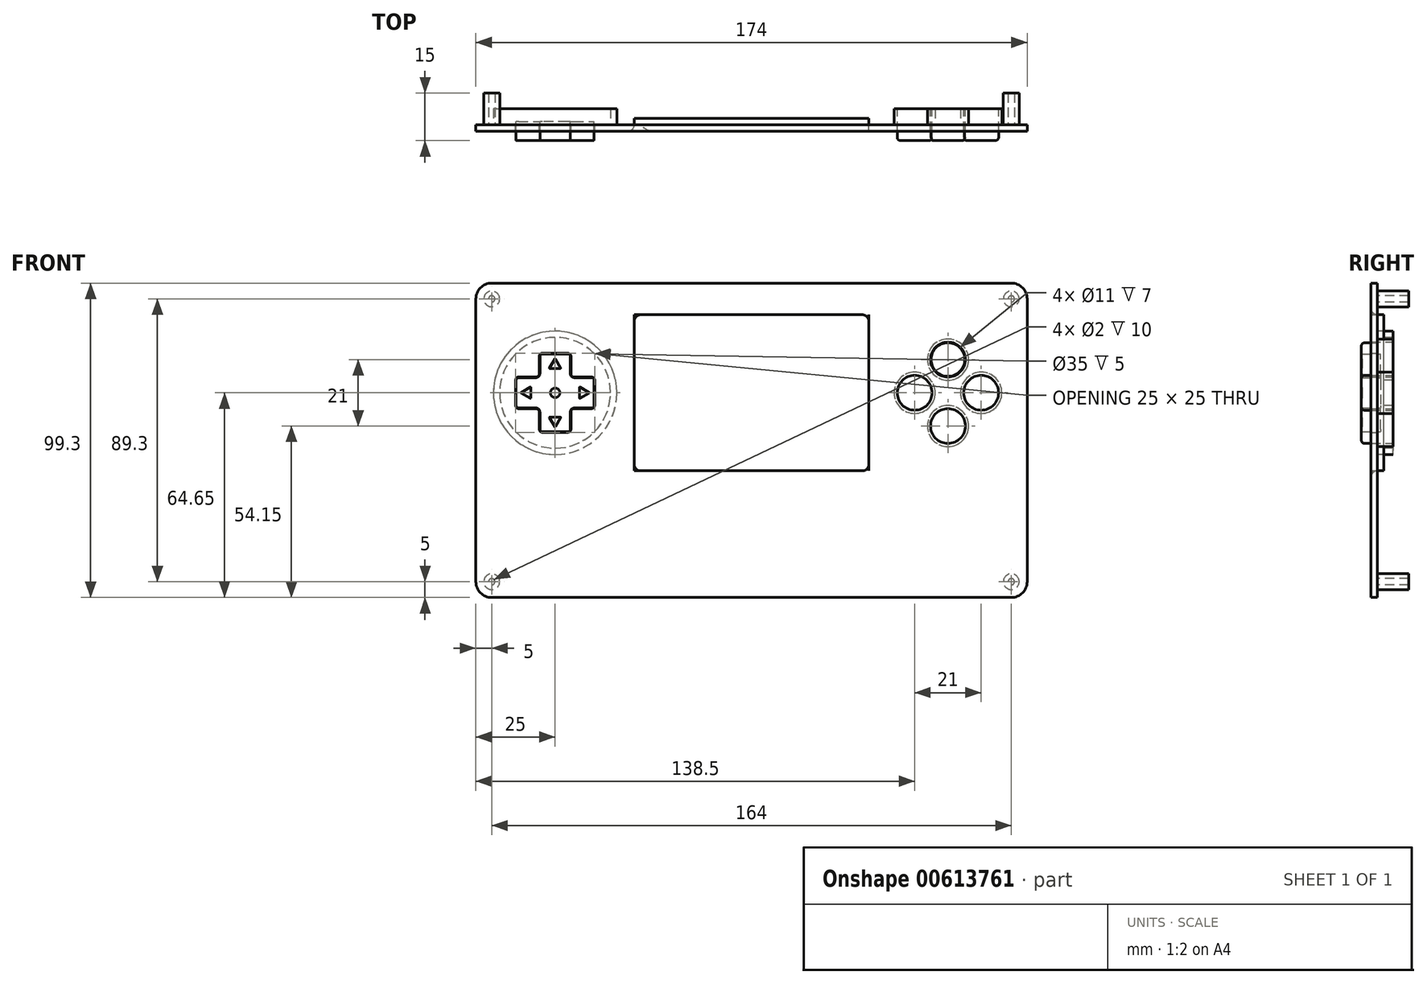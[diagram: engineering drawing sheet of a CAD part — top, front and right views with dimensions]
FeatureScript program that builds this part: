
annotation { "Feature Type Name" : "Feature", "Feature Type Description" : "" }
export const myFeature = defineFeature(function(context is Context, id is Id, definition is map)
    precondition{}
    {
        {
            var Q0;
            Q0=qCreatedBy(makeId("Front.planeOp"),FACE);
            var sketch = newSketch(context, id + "F0", { "sketchPlane" : qUnion([Q0])});
            skLineSegment(sketch, "E0.bottom", {"start": v(37, -24.65) * mm, "end": v(-37, -24.65) * mm});
            skLineSegment(sketch, "E0.top", {"start": v(37, 24.65) * mm, "end": v(-37, 24.65) * mm});
            skLineSegment(sketch, "E0.left", {"start": v(37, -24.65) * mm, "end": v(37, 24.65) * mm});
            skLineSegment(sketch, "E0.right", {"start": v(-37, -24.65) * mm, "end": v(-37, 24.65) * mm});
            skPoint(sketch, "E0.middle", {"position": v(0, 0) * mm});
            skLineSegment(sketch, "E1", {"start": v(-77.18, 0) * mm, "end": v(-77.18, 0) * mm});
            skPoint(sketch, "E1.startSnap0", {"position": v(-37, 0) * mm});
            skPoint(sketch, "E1.endSnap0", {"position": v(37, 0) * mm});
            skLineSegment(sketch, "E2.bottom", {"start": v(-57, -12.5) * mm, "end": v(-67, -12.5) * mm});
            skLineSegment(sketch, "E2.top", {"start": v(-57, 12.5) * mm, "end": v(-67, 12.5) * mm});
            skLineSegment(sketch, "E2.left", {"start": v(-57, -12.5) * mm, "end": v(-57, 12.5) * mm});
            skLineSegment(sketch, "E2.right", {"start": v(-67, -12.5) * mm, "end": v(-67, 12.5) * mm});
            skPoint(sketch, "E2.middle", {"position": v(-62, 0) * mm});
            skLineSegment(sketch, "E3.bottom", {"start": v(-74.5, 5) * mm, "end": v(-49.5, 5) * mm});
            skLineSegment(sketch, "E3.top", {"start": v(-74.5, -5) * mm, "end": v(-49.5, -5) * mm});
            skLineSegment(sketch, "E3.left", {"start": v(-74.5, 5) * mm, "end": v(-74.5, -5) * mm});
            skLineSegment(sketch, "E3.right", {"start": v(-49.5, 5) * mm, "end": v(-49.5, -5) * mm});
            skLineSegment(sketch, "E4", {"start": v(-67, 12.5) * mm, "end": v(80.57, 12.5) * mm, "construction": true});
            skLineSegment(sketch, "E5", {"start": v(37, 0) * mm, "end": v(62, 0) * mm, "construction": true});
            skLineSegment(sketch, "E6", {"start": v(62, 0) * mm, "end": v(62, 12.5) * mm, "construction": true});
            skCircle(sketch, "E7", {"center": v(-62, 0) * mm, "radius": 17.5 * mm});
            skLineSegment(sketch, "E8.bottom", {"start": v(-87, 34.65) * mm, "end": v(87, 34.65) * mm});
            skLineSegment(sketch, "E8.top", {"start": v(-87, -64.65) * mm, "end": v(87, -64.65) * mm});
            skLineSegment(sketch, "E8.left", {"start": v(-87, 34.65) * mm, "end": v(-87, -64.65) * mm});
            skLineSegment(sketch, "E8.right", {"start": v(87, 34.65) * mm, "end": v(87, -64.65) * mm});
            skPoint(sketch, "E9.center.orphan", {"position": v(62, 6.25) * mm});
            skCircle(sketch, "E10", {"center": v(62, 10.5) * mm, "radius": 5.5 * mm});
            skCircle(sketch, "E11.1.0", {"center": v(51.5, 0) * mm, "radius": 5.5 * mm});
            skCircle(sketch, "E11.2.0", {"center": v(62, -10.5) * mm, "radius": 5.5 * mm});
            skCircle(sketch, "E11.3.0", {"center": v(72.5, 0) * mm, "radius": 5.5 * mm});
            skPoint(sketch, "E11.center", {"position": v(62, 0) * mm});
            skSolve(sketch);
        }
        {
            var Q0;
            Q0=makeQuery(id+"F0.imprint","IMPRINT",FACE,{"disambiguationData":[TD([[makeQuery(id+"F0.imprint","IMPRINT",EDGE,{"derivedFrom":sQuery(id+"F0.wireOp",EDGE,"E0.bottom")}),1.0]])]});
            var Q1;
            {var subQ8=sQuery(id+"F0.wireOp",EDGE,"E2.bottom");Q1=makeQuery(id+"F0.imprint","IMPRINT",FACE,{"disambiguationData":[TD([[makeQuery(id+"F0.imprint","IMPRINT",EDGE,{"derivedFrom":subQ8}),1.0]])]});}
            extrude(context, id + "F1", {"entities" : qUnion([Q0, Q1]), "depth" : 2 * mm, "offsetDistance" : 25 * mm});
        }
        {
            var Q0;
            Q0=makeQuery(id+"F1.opExtrude","SWEPT_EDGE",EDGE,{"disambiguationData":[OSD([sQuery(id+"F0.wireOp",EDGE,"E2.top"),sQuery(id+"F0.wireOp",EDGE,"E2.right")])]});
            var Q1;
            Q1=makeQuery(id+"F1.opExtrude","SWEPT_EDGE",EDGE,{"disambiguationData":[OSD([sQuery(id+"F0.wireOp",EDGE,"E2.right"),sQuery(id+"F0.wireOp",EDGE,"E3.bottom")])]});
            var Q2;
            Q2=makeQuery(id+"F1.opExtrude","SWEPT_EDGE",EDGE,{"disambiguationData":[OSD([sQuery(id+"F0.wireOp",EDGE,"E3.bottom"),sQuery(id+"F0.wireOp",EDGE,"E3.left")])]});
            var Q3;
            Q3=makeQuery(id+"F1.opExtrude","SWEPT_EDGE",EDGE,{"disambiguationData":[OSD([sQuery(id+"F0.wireOp",EDGE,"E3.top"),sQuery(id+"F0.wireOp",EDGE,"E3.left")])]});
            var Q4;
            Q4=makeQuery(id+"F1.opExtrude","SWEPT_EDGE",EDGE,{"disambiguationData":[OSD([sQuery(id+"F0.wireOp",EDGE,"E2.right"),sQuery(id+"F0.wireOp",EDGE,"E3.top")])]});
            var Q5;
            Q5=makeQuery(id+"F1.opExtrude","SWEPT_EDGE",EDGE,{"disambiguationData":[OSD([sQuery(id+"F0.wireOp",EDGE,"E2.bottom"),sQuery(id+"F0.wireOp",EDGE,"E2.right")])]});
            var Q6;
            Q6=makeQuery(id+"F1.opExtrude","SWEPT_EDGE",EDGE,{"disambiguationData":[OSD([sQuery(id+"F0.wireOp",EDGE,"E2.bottom"),sQuery(id+"F0.wireOp",EDGE,"E2.left")])]});
            var Q7;
            Q7=makeQuery(id+"F1.opExtrude","SWEPT_EDGE",EDGE,{"disambiguationData":[OSD([sQuery(id+"F0.wireOp",EDGE,"E2.left"),sQuery(id+"F0.wireOp",EDGE,"E3.top")])]});
            var Q8;
            Q8=makeQuery(id+"F1.opExtrude","SWEPT_EDGE",EDGE,{"disambiguationData":[OSD([sQuery(id+"F0.wireOp",EDGE,"E3.top"),sQuery(id+"F0.wireOp",EDGE,"E3.right")])]});
            var Q9;
            Q9=makeQuery(id+"F1.opExtrude","SWEPT_EDGE",EDGE,{"disambiguationData":[OSD([sQuery(id+"F0.wireOp",EDGE,"E3.bottom"),sQuery(id+"F0.wireOp",EDGE,"E3.right")])]});
            var Q10;
            Q10=makeQuery(id+"F1.opExtrude","SWEPT_EDGE",EDGE,{"disambiguationData":[OSD([sQuery(id+"F0.wireOp",EDGE,"E2.left"),sQuery(id+"F0.wireOp",EDGE,"E3.bottom")])]});
            var Q11;
            Q11=makeQuery(id+"F1.opExtrude","SWEPT_EDGE",EDGE,{"disambiguationData":[OSD([sQuery(id+"F0.wireOp",EDGE,"E2.top"),sQuery(id+"F0.wireOp",EDGE,"E2.left")])]});
            fillet(context, id + "F2", {"entities" : qUnion([Q0, Q1, Q2, Q3, Q4, Q5, Q6, Q7, Q8, Q9, Q10, Q11]), "radius" : 1 * mm, "tangentPropagation" : true, "allowEdgeOverflow" : false});
        }
        {
            var Q0;
            Q0=makeQuery(id+"F1.opExtrude","SWEPT_EDGE",EDGE,{"disambiguationData":[OSD([sQuery(id+"F0.wireOp",EDGE,"E8.bottom"),sQuery(id+"F0.wireOp",EDGE,"E8.right")])]});
            var Q1;
            Q1=makeQuery(id+"F1.opExtrude","SWEPT_EDGE",EDGE,{"disambiguationData":[OSD([sQuery(id+"F0.wireOp",EDGE,"E8.top"),sQuery(id+"F0.wireOp",EDGE,"E8.right")])]});
            var Q2;
            Q2=makeQuery(id+"F1.opExtrude","SWEPT_EDGE",EDGE,{"disambiguationData":[OSD([sQuery(id+"F0.wireOp",EDGE,"E8.bottom"),sQuery(id+"F0.wireOp",EDGE,"E8.left")])]});
            var Q3;
            Q3=makeQuery(id+"F1.opExtrude","SWEPT_EDGE",EDGE,{"disambiguationData":[OSD([sQuery(id+"F0.wireOp",EDGE,"E8.top"),sQuery(id+"F0.wireOp",EDGE,"E8.left")])]});
            fillet(context, id + "F3", {"entities" : qUnion([Q0, Q1, Q2, Q3]), "radius" : 5 * mm, "tangentPropagation" : true, "allowEdgeOverflow" : false});
        }
        {
            var Q0;
            Q0=makeQuery(id+"F1.opExtrude","CAP_FACE",FACE,{"disambiguationData":[OSD([sQuery(id+"F0.wireOp",EDGE,"E0.bottom"),sQuery(id+"F0.wireOp",EDGE,"E0.top"),sQuery(id+"F0.wireOp",EDGE,"E0.left"),sQuery(id+"F0.wireOp",EDGE,"E0.right"),sQuery(id+"F0.wireOp",EDGE,"E2.bottom"),sQuery(id+"F0.wireOp",EDGE,"E2.top"),sQuery(id+"F0.wireOp",EDGE,"E2.left"),sQuery(id+"F0.wireOp",EDGE,"E2.right"),sQuery(id+"F0.wireOp",EDGE,"E3.bottom"),sQuery(id+"F0.wireOp",EDGE,"E3.top"),sQuery(id+"F0.wireOp",EDGE,"E3.left"),sQuery(id+"F0.wireOp",EDGE,"E3.right"),sQuery(id+"F0.wireOp",EDGE,"E8.bottom"),sQuery(id+"F0.wireOp",EDGE,"E8.top"),sQuery(id+"F0.wireOp",EDGE,"E8.left"),sQuery(id+"F0.wireOp",EDGE,"E8.right"),sQuery(id+"F0.wireOp",EDGE,"E10"),sQuery(id+"F0.wireOp",EDGE,"E11.1.0"),sQuery(id+"F0.wireOp",EDGE,"E11.2.0"),sQuery(id+"F0.wireOp",EDGE,"E11.3.0")])],"isStart":true});
            var sketch = newSketch(context, id + "F4", { "sketchPlane" : qUnion([Q0])});
            skCircle(sketch, "E12.0", {"center": v(-62, 10.5) * mm, "radius": 6.5 * mm});
            skCircle(sketch, "E13.0", {"center": v(-72.5, 0) * mm, "radius": 6.5 * mm});
            skCircle(sketch, "E14.0", {"center": v(-51.5, 0) * mm, "radius": 6.5 * mm});
            skCircle(sketch, "E15.0", {"center": v(-62, -10.5) * mm, "radius": 6.5 * mm});
            skSolve(sketch);
        }
        {
            var Q0;
            Q0=makeQuery(id+"F4.imprint","IMPRINT",FACE,{"disambiguationData":[TD([[makeQuery(id+"F4.imprint","IMPRINT",EDGE,{"derivedFrom":sQuery(id+"F4.wireOp",EDGE,"E12.0")}),1.0]])]});
            var Q1;
            Q1=makeQuery(id+"F4.imprint","IMPRINT",FACE,{"disambiguationData":[TD([[makeQuery(id+"F4.imprint","IMPRINT",EDGE,{"derivedFrom":sQuery(id+"F4.wireOp",EDGE,"E13.0")}),1.0]])]});
            var Q2;
            Q2=makeQuery(id+"F4.imprint","IMPRINT",FACE,{"disambiguationData":[TD([[makeQuery(id+"F4.imprint","IMPRINT",EDGE,{"derivedFrom":sQuery(id+"F4.wireOp",EDGE,"E14.0")}),1.0]])]});
            var Q3;
            Q3=makeQuery(id+"F4.imprint","IMPRINT",FACE,{"disambiguationData":[TD([[makeQuery(id+"F4.imprint","IMPRINT",EDGE,{"derivedFrom":sQuery(id+"F4.wireOp",EDGE,"E15.0")}),1.0]])]});
            extrude(context, id + "F5", {"entities" : qUnion([Q0, Q1, Q2, Q3]), "operationType" : NewBodyOperationType.ADD, "depth" : 5 * mm, "offsetDistance" : 25 * mm});
        }
        {
            var Q0;
            Q0=makeQuery(id+"F0.imprint","IMPRINT",FACE,{"disambiguationData":[TD([[makeQuery(id+"F0.imprint","IMPRINT",EDGE,{"derivedFrom":sQuery(id+"F0.wireOp",EDGE,"E0.bottom")}),1.0]])]});
            var sketch = newSketch(context, id + "F6", { "sketchPlane" : qUnion([Q0])});
            skCircle(sketch, "E16.0", {"center": v(-62, 0) * mm, "radius": 19.5 * mm});
            skCircle(sketch, "E17.0", {"center": v(-62, 0) * mm, "radius": 17.5 * mm});
            skSolve(sketch);
        }
        {
            var Q0;
            Q0 = qSketchRegion(id + "F6", true);
            var Q1;
            Q1=makeQuery(id+"F5.opExtrude","CAP_FACE",FACE,{"disambiguationData":[OSD([sQuery(id+"F0.wireOp",EDGE,"E11.1.0"),sQuery(id+"F4.wireOp",EDGE,"E14.0")])],"isStart":false});
            extrude(context, id + "F7", {"entities" : qUnion([Q0]), "operationType" : NewBodyOperationType.ADD, "endBound" : BoundingType.UP_TO_SURFACE, "oppositeDirection" : true, "depth" : 25 * mm, "endBoundEntityFace" : qUnion([Q1]), "offsetDistance" : 25 * mm});
        }
        {
            var Q0;
            Q0=makeQuery(id+"F1.opExtrude","SWEPT_EDGE",EDGE,{"disambiguationData":[OSD([sQuery(id+"F0.wireOp",EDGE,"E0.top"),sQuery(id+"F0.wireOp",EDGE,"E0.right")])]});
            var Q1;
            Q1=makeQuery(id+"F1.opExtrude","SWEPT_EDGE",EDGE,{"disambiguationData":[OSD([sQuery(id+"F0.wireOp",EDGE,"E0.top"),sQuery(id+"F0.wireOp",EDGE,"E0.left")])]});
            var Q2;
            Q2=makeQuery(id+"F1.opExtrude","SWEPT_EDGE",EDGE,{"disambiguationData":[OSD([sQuery(id+"F0.wireOp",EDGE,"E0.bottom"),sQuery(id+"F0.wireOp",EDGE,"E0.left")])]});
            var Q3;
            Q3=makeQuery(id+"F1.opExtrude","SWEPT_EDGE",EDGE,{"disambiguationData":[OSD([sQuery(id+"F0.wireOp",EDGE,"E0.bottom"),sQuery(id+"F0.wireOp",EDGE,"E0.right")])]});
            var Q4;
            Q4=makeQuery(id+"F1.opExtrude","CAP_EDGE",EDGE,{"disambiguationData":[OSD([sQuery(id+"F0.wireOp",EDGE,"E0.right")])],"isStart":false});
            fillet(context, id + "F8", {"entities" : qUnion([Q0, Q1, Q2, Q3, Q4]), "radius" : 2 * mm, "tangentPropagation" : true, "allowEdgeOverflow" : false});
        }
        {
            var Q0;
            Q0=makeQuery(id+"F0.imprint","IMPRINT",FACE,{"disambiguationData":[TD([[makeQuery(id+"F0.imprint","IMPRINT",EDGE,{"derivedFrom":sQuery(id+"F0.wireOp",EDGE,"E0.bottom")}),1.0]])]});
            var sketch = newSketch(context, id + "F9", { "sketchPlane" : qUnion([Q0])});
            skLineSegment(sketch, "E18.0", {"start": v(-82, 29.65) * mm, "end": v(-82, -59.65) * mm, "construction": true});
            skLineSegment(sketch, "E18.1", {"start": v(82, 29.65) * mm, "end": v(-82, 29.65) * mm, "construction": true});
            skLineSegment(sketch, "E18.2", {"start": v(82, -59.65) * mm, "end": v(82, 29.65) * mm, "construction": true});
            skLineSegment(sketch, "E18.3", {"start": v(-82, -59.65) * mm, "end": v(82, -59.65) * mm, "construction": true});
            skCircle(sketch, "E19", {"center": v(82, 29.65) * mm, "radius": 1 * mm});
            skCircle(sketch, "E20", {"center": v(-82, 29.65) * mm, "radius": 1 * mm});
            skCircle(sketch, "E21", {"center": v(-82, -59.65) * mm, "radius": 1 * mm});
            skCircle(sketch, "E22", {"center": v(82, -59.65) * mm, "radius": 1 * mm});
            skCircle(sketch, "E23", {"center": v(82, -59.65) * mm, "radius": 2.5 * mm});
            skCircle(sketch, "E24", {"center": v(82, 29.65) * mm, "radius": 2.5 * mm});
            skCircle(sketch, "E25", {"center": v(-82, 29.65) * mm, "radius": 2.5 * mm});
            skCircle(sketch, "E26", {"center": v(-82, -59.65) * mm, "radius": 2.5 * mm});
            skSolve(sketch);
        }
        {
            var Q0;
            Q0=makeQuery(id+"F9.imprint","IMPRINT",FACE,{"disambiguationData":[TD([[makeQuery(id+"F9.imprint","IMPRINT",EDGE,{"derivedFrom":sQuery(id+"F9.wireOp",EDGE,"E19")}),-1.0]])]});
            var Q1;
            Q1=makeQuery(id+"F9.imprint","IMPRINT",FACE,{"disambiguationData":[TD([[makeQuery(id+"F9.imprint","IMPRINT",EDGE,{"derivedFrom":sQuery(id+"F9.wireOp",EDGE,"E20")}),-1.0]])]});
            var Q2;
            Q2=makeQuery(id+"F9.imprint","IMPRINT",FACE,{"disambiguationData":[TD([[makeQuery(id+"F9.imprint","IMPRINT",EDGE,{"derivedFrom":sQuery(id+"F9.wireOp",EDGE,"E21")}),-1.0]])]});
            var Q3;
            Q3=makeQuery(id+"F9.imprint","IMPRINT",FACE,{"disambiguationData":[TD([[makeQuery(id+"F9.imprint","IMPRINT",EDGE,{"derivedFrom":sQuery(id+"F9.wireOp",EDGE,"E22")}),-1.0]])]});
            extrude(context, id + "F10", {"entities" : qUnion([Q0, Q1, Q2, Q3]), "operationType" : NewBodyOperationType.ADD, "oppositeDirection" : true, "depth" : 10 * mm, "offsetDistance" : 25 * mm});
        }
        {
            var Q0;
            Q0=makeQuery(id+"F0.imprint","IMPRINT",FACE,{"disambiguationData":[TD([[makeQuery(id+"F0.imprint","IMPRINT",EDGE,{"derivedFrom":sQuery(id+"F0.wireOp",EDGE,"E0.bottom")}),-1.0]])]});
            extrude(context, id + "F11", {"entities" : qUnion([Q0]), "oppositeDirection" : true, "depth" : 2 * mm, "offsetDistance" : 25 * mm});
        }
        {
            var Q0;
            Q0=makeQuery(id+"F1.opExtrude","CAP_FACE",FACE,{"disambiguationData":[OSD([sQuery(id+"F0.wireOp",EDGE,"E0.bottom"),sQuery(id+"F0.wireOp",EDGE,"E0.top"),sQuery(id+"F0.wireOp",EDGE,"E0.left"),sQuery(id+"F0.wireOp",EDGE,"E0.right"),sQuery(id+"F0.wireOp",EDGE,"E2.bottom"),sQuery(id+"F0.wireOp",EDGE,"E2.top"),sQuery(id+"F0.wireOp",EDGE,"E2.left"),sQuery(id+"F0.wireOp",EDGE,"E2.right"),sQuery(id+"F0.wireOp",EDGE,"E3.bottom"),sQuery(id+"F0.wireOp",EDGE,"E3.top"),sQuery(id+"F0.wireOp",EDGE,"E3.left"),sQuery(id+"F0.wireOp",EDGE,"E3.right"),sQuery(id+"F0.wireOp",EDGE,"E8.bottom"),sQuery(id+"F0.wireOp",EDGE,"E8.top"),sQuery(id+"F0.wireOp",EDGE,"E8.left"),sQuery(id+"F0.wireOp",EDGE,"E8.right"),sQuery(id+"F0.wireOp",EDGE,"E10"),sQuery(id+"F0.wireOp",EDGE,"E11.1.0"),sQuery(id+"F0.wireOp",EDGE,"E11.2.0"),sQuery(id+"F0.wireOp",EDGE,"E11.3.0")])],"isStart":false});
            var sketch = newSketch(context, id + "F12", { "sketchPlane" : qUnion([Q0])});
            skArc(sketch, "E27.0", {"start": v(-68, 4.8) * mm, "mid": v(-67.15, 5.15) * mm, "end": v(-66.8, 6) * mm});
            skLineSegment(sketch, "E27.1", {"start": v(-56, -4.8) * mm, "end": v(-50.5, -4.8) * mm});
            skArc(sketch, "E27.2", {"start": v(-49.7, -4) * mm, "mid": v(-49.93, -4.57) * mm, "end": v(-50.5, -4.8) * mm});
            skLineSegment(sketch, "E27.3", {"start": v(-49.7, 4) * mm, "end": v(-49.7, -4) * mm});
            skArc(sketch, "E27.4", {"start": v(-50.5, 4.8) * mm, "mid": v(-49.93, 4.57) * mm, "end": v(-49.7, 4) * mm});
            skLineSegment(sketch, "E27.5", {"start": v(-56, 4.8) * mm, "end": v(-50.5, 4.8) * mm});
            skArc(sketch, "E27.6", {"start": v(-57.2, 6) * mm, "mid": v(-56.85, 5.15) * mm, "end": v(-56, 4.8) * mm});
            skArc(sketch, "E27.7", {"start": v(-66.8, 11.5) * mm, "mid": v(-66.57, 12.07) * mm, "end": v(-66, 12.3) * mm});
            skLineSegment(sketch, "E27.8", {"start": v(-58, 12.3) * mm, "end": v(-66, 12.3) * mm});
            skArc(sketch, "E27.9", {"start": v(-58, 12.3) * mm, "mid": v(-57.43, 12.07) * mm, "end": v(-57.2, 11.5) * mm});
            skLineSegment(sketch, "E27.10", {"start": v(-57.2, 6) * mm, "end": v(-57.2, 11.5) * mm});
            skArc(sketch, "E27.11", {"start": v(-56, -4.8) * mm, "mid": v(-56.85, -5.15) * mm, "end": v(-57.2, -6) * mm});
            skLineSegment(sketch, "E27.12", {"start": v(-66.8, 6) * mm, "end": v(-66.8, 11.5) * mm});
            skLineSegment(sketch, "E27.13", {"start": v(-57.2, -11.5) * mm, "end": v(-57.2, -6) * mm});
            skArc(sketch, "E27.14", {"start": v(-57.2, -11.5) * mm, "mid": v(-57.43, -12.07) * mm, "end": v(-58, -12.3) * mm});
            skLineSegment(sketch, "E27.15", {"start": v(-58, -12.3) * mm, "end": v(-66, -12.3) * mm});
            skArc(sketch, "E27.16", {"start": v(-66, -12.3) * mm, "mid": v(-66.57, -12.07) * mm, "end": v(-66.8, -11.5) * mm});
            skLineSegment(sketch, "E27.17", {"start": v(-66.8, -11.5) * mm, "end": v(-66.8, -6) * mm});
            skArc(sketch, "E27.18", {"start": v(-66.8, -6) * mm, "mid": v(-67.15, -5.15) * mm, "end": v(-68, -4.8) * mm});
            skLineSegment(sketch, "E27.19", {"start": v(-73.5, -4.8) * mm, "end": v(-68, -4.8) * mm});
            skArc(sketch, "E27.20", {"start": v(-73.5, -4.8) * mm, "mid": v(-74.07, -4.57) * mm, "end": v(-74.3, -4) * mm});
            skLineSegment(sketch, "E27.21", {"start": v(-74.3, 4) * mm, "end": v(-74.3, -4) * mm});
            skArc(sketch, "E27.22", {"start": v(-74.3, 4) * mm, "mid": v(-74.07, 4.57) * mm, "end": v(-73.5, 4.8) * mm});
            skLineSegment(sketch, "E27.23", {"start": v(-73.5, 4.8) * mm, "end": v(-68, 4.8) * mm});
            skSolve(sketch);
        }
        {
            var Q0;
            Q0=makeQuery(id+"F12.imprint","IMPRINT",FACE,{"disambiguationData":[TD([[makeQuery(id+"F12.imprint","IMPRINT",EDGE,{"derivedFrom":sQuery(id+"F12.wireOp",EDGE,"E27.0")}),-1.0]])]});
            extrude(context, id + "F13", {"entities" : qUnion([Q0]), "depth" : 3 * mm, "offsetDistance" : 25 * mm, "hasSecondDirection" : true, "secondDirectionOppositeDirection" : true, "secondDirectionDepth" : 3 * mm});
        }
        {
            var Q0;
            Q0=makeQuery(id+"F1.opExtrude","CAP_FACE",FACE,{"disambiguationData":[OSD([sQuery(id+"F0.wireOp",EDGE,"E0.bottom"),sQuery(id+"F0.wireOp",EDGE,"E0.top"),sQuery(id+"F0.wireOp",EDGE,"E0.left"),sQuery(id+"F0.wireOp",EDGE,"E0.right"),sQuery(id+"F0.wireOp",EDGE,"E2.bottom"),sQuery(id+"F0.wireOp",EDGE,"E2.top"),sQuery(id+"F0.wireOp",EDGE,"E2.left"),sQuery(id+"F0.wireOp",EDGE,"E2.right"),sQuery(id+"F0.wireOp",EDGE,"E3.bottom"),sQuery(id+"F0.wireOp",EDGE,"E3.top"),sQuery(id+"F0.wireOp",EDGE,"E3.left"),sQuery(id+"F0.wireOp",EDGE,"E3.right"),sQuery(id+"F0.wireOp",EDGE,"E8.bottom"),sQuery(id+"F0.wireOp",EDGE,"E8.top"),sQuery(id+"F0.wireOp",EDGE,"E8.left"),sQuery(id+"F0.wireOp",EDGE,"E8.right"),sQuery(id+"F0.wireOp",EDGE,"E10"),sQuery(id+"F0.wireOp",EDGE,"E11.1.0"),sQuery(id+"F0.wireOp",EDGE,"E11.2.0"),sQuery(id+"F0.wireOp",EDGE,"E11.3.0")])],"isStart":false});
            var sketch = newSketch(context, id + "F14", { "sketchPlane" : qUnion([Q0])});
            skCircle(sketch, "E28.0", {"center": v(62, 10.5) * mm, "radius": 5.3 * mm});
            skCircle(sketch, "E29.0", {"center": v(51.5, 0) * mm, "radius": 5.7 * mm});
            skCircle(sketch, "E30.0", {"center": v(72.5, 0) * mm, "radius": 5.7 * mm});
            skCircle(sketch, "E31.0", {"center": v(62, -10.5) * mm, "radius": 5.7 * mm});
            skSolve(sketch);
        }
        {
            var Q0;
            Q0=makeQuery(id+"F14.imprint","IMPRINT",FACE,{"disambiguationData":[TD([[makeQuery(id+"F14.imprint","IMPRINT",EDGE,{"derivedFrom":sQuery(id+"F14.wireOp",EDGE,"E28.0")}),1.0]])]});
            var Q1;
            Q1=makeQuery(id+"F14.imprint","IMPRINT",FACE,{"disambiguationData":[TD([[makeQuery(id+"F14.imprint","IMPRINT",EDGE,{"derivedFrom":makeQuery(id+"F1.opExtrude","CAP_EDGE",EDGE,{"disambiguationData":[OSD([sQuery(id+"F0.wireOp",EDGE,"E11.1.0")])],"isStart":false})}),1.0]])]});
            var Q2;
            Q2=makeQuery(id+"F14.imprint","IMPRINT",FACE,{"disambiguationData":[TD([[makeQuery(id+"F14.imprint","IMPRINT",EDGE,{"derivedFrom":makeQuery(id+"F1.opExtrude","CAP_EDGE",EDGE,{"disambiguationData":[OSD([sQuery(id+"F0.wireOp",EDGE,"E11.3.0")])],"isStart":false})}),1.0]])]});
            var Q3;
            Q3=makeQuery(id+"F14.imprint","IMPRINT",FACE,{"disambiguationData":[TD([[makeQuery(id+"F14.imprint","IMPRINT",EDGE,{"derivedFrom":makeQuery(id+"F1.opExtrude","CAP_EDGE",EDGE,{"disambiguationData":[OSD([sQuery(id+"F0.wireOp",EDGE,"E11.2.0")])],"isStart":false})}),1.0]])]});
            extrude(context, id + "F15", {"entities" : qUnion([Q0, Q1, Q2, Q3]), "depth" : 3 * mm, "offsetDistance" : 25 * mm, "hasSecondDirection" : true, "secondDirectionOppositeDirection" : true, "secondDirectionDepth" : 2 * mm});
        }
        {
            var Q0;
            Q0=makeQuery(id+"F15.opExtrude","CAP_EDGE",EDGE,{"disambiguationData":[OSD([sQuery(id+"F14.wireOp",EDGE,"E28.0")])],"isStart":false});
            var Q1;
            Q1=makeQuery(id+"F15.opExtrude","CAP_EDGE",EDGE,{"disambiguationData":[OSD([sQuery(id+"F0.wireOp",EDGE,"E11.1.0")])],"isStart":false});
            var Q2;
            Q2=makeQuery(id+"F15.opExtrude","CAP_EDGE",EDGE,{"disambiguationData":[OSD([sQuery(id+"F0.wireOp",EDGE,"E11.3.0")])],"isStart":false});
            var Q3;
            Q3=makeQuery(id+"F15.opExtrude","CAP_FACE",FACE,{"disambiguationData":[OSD([sQuery(id+"F0.wireOp",EDGE,"E11.2.0")])],"isStart":false});
            fillet(context, id + "F16", {"entities" : qUnion([Q0, Q1, Q2, Q3]), "radius" : 1 * mm, "tangentPropagation" : true, "allowEdgeOverflow" : false});
        }
        {
            var Q0;
            Q0=makeQuery(id+"F13.opExtrude","CAP_FACE",FACE,{"disambiguationData":[OSD([sQuery(id+"F12.wireOp",EDGE,"E27.0"),sQuery(id+"F12.wireOp",EDGE,"E27.1"),sQuery(id+"F12.wireOp",EDGE,"E27.2"),sQuery(id+"F12.wireOp",EDGE,"E27.3"),sQuery(id+"F12.wireOp",EDGE,"E27.4"),sQuery(id+"F12.wireOp",EDGE,"E27.5"),sQuery(id+"F12.wireOp",EDGE,"E27.6"),sQuery(id+"F12.wireOp",EDGE,"E27.7"),sQuery(id+"F12.wireOp",EDGE,"E27.8"),sQuery(id+"F12.wireOp",EDGE,"E27.9"),sQuery(id+"F12.wireOp",EDGE,"E27.10"),sQuery(id+"F12.wireOp",EDGE,"E27.11"),sQuery(id+"F12.wireOp",EDGE,"E27.12"),sQuery(id+"F12.wireOp",EDGE,"E27.13"),sQuery(id+"F12.wireOp",EDGE,"E27.14"),sQuery(id+"F12.wireOp",EDGE,"E27.15"),sQuery(id+"F12.wireOp",EDGE,"E27.16"),sQuery(id+"F12.wireOp",EDGE,"E27.17"),sQuery(id+"F12.wireOp",EDGE,"E27.18"),sQuery(id+"F12.wireOp",EDGE,"E27.19"),sQuery(id+"F12.wireOp",EDGE,"E27.20"),sQuery(id+"F12.wireOp",EDGE,"E27.21"),sQuery(id+"F12.wireOp",EDGE,"E27.22"),sQuery(id+"F12.wireOp",EDGE,"E27.23")])],"isStart":false});
            var sketch = newSketch(context, id + "F17", { "sketchPlane" : qUnion([Q0])});
            skLineSegment(sketch, "E32", {"start": v(-74.3, 0) * mm, "end": v(-49.7, 0) * mm, "construction": true});
            skLineSegment(sketch, "E33", {"start": v(-62, 12.3) * mm, "end": v(-62, -12.3) * mm, "construction": true});
            skLineSegment(sketch, "E34.cCircle", {"start": v(-62, 6.6) * mm, "end": v(-62, 6.6) * mm});
            skPoint(sketch, "E34.cCircle.centerSnap0", {"position": v(-57.2, 8.75) * mm});
            skLineSegment(sketch, "E34.1", {"start": v(-62, 6.6) * mm, "end": v(-62, 6.6) * mm});
            skPoint(sketch, "E34.0.midPoint", {"position": v(-60.14, 9.82) * mm});
            skCircle(sketch, "E35.cCircle", {"center": v(-53.25, 0) * mm, "radius": 1.07 * mm, "construction": true});
            skPoint(sketch, "E35.cCircle.centerSnap0", {"position": v(-53.25, -4.8) * mm});
            skLineSegment(sketch, "E35.0", {"start": v(-54.32, -1.86) * mm, "end": v(-54.32, 1.86) * mm});
            skLineSegment(sketch, "E35.1", {"start": v(-54.32, 1.86) * mm, "end": v(-51.1, 0) * mm});
            skLineSegment(sketch, "E35.2", {"start": v(-51.1, 0) * mm, "end": v(-54.32, -1.86) * mm});
            skPoint(sketch, "E35.0.midPoint", {"position": v(-54.32, 0) * mm});
            skPoint(sketch, "E36.orphan", {"position": v(-65.72, 6.6) * mm});
            skPoint(sketch, "E37.orphan", {"position": v(-58.28, 6.6) * mm});
            skPoint(sketch, "E34.2.end.orphan", {"position": v(-62, 13.04) * mm});
            skLineSegment(sketch, "E38.1.0", {"start": v(-63.86, 7.68) * mm, "end": v(-62, 10.9) * mm});
            skLineSegment(sketch, "E38.1.1", {"start": v(-60.14, 7.68) * mm, "end": v(-63.86, 7.68) * mm});
            skLineSegment(sketch, "E38.1.2", {"start": v(-62, 10.9) * mm, "end": v(-60.14, 7.68) * mm});
            skLineSegment(sketch, "E38.2.0", {"start": v(-69.68, -1.86) * mm, "end": v(-72.9, 0) * mm});
            skLineSegment(sketch, "E38.2.1", {"start": v(-69.68, 1.86) * mm, "end": v(-69.68, -1.86) * mm});
            skLineSegment(sketch, "E38.2.2", {"start": v(-72.9, 0) * mm, "end": v(-69.68, 1.86) * mm});
            skLineSegment(sketch, "E38.3.0", {"start": v(-60.14, -7.68) * mm, "end": v(-62, -10.9) * mm});
            skLineSegment(sketch, "E38.3.1", {"start": v(-63.86, -7.68) * mm, "end": v(-60.14, -7.68) * mm});
            skLineSegment(sketch, "E38.3.2", {"start": v(-62, -10.9) * mm, "end": v(-63.86, -7.68) * mm});
            skPoint(sketch, "E38.center", {"position": v(-62, 0) * mm});
            skCircle(sketch, "E39", {"center": v(-62, 0) * mm, "radius": 1.5 * mm});
            skSolve(sketch);
        }
        {
            var Q0;
            Q0=makeQuery(id+"F17.imprint","IMPRINT",FACE,{"disambiguationData":[TD([[makeQuery(id+"F17.imprint","IMPRINT",EDGE,{"derivedFrom":sQuery(id+"F17.wireOp",EDGE,"E38.1.0")}),-1.0]])]});
            var Q1;
            Q1=makeQuery(id+"F17.imprint","IMPRINT",FACE,{"disambiguationData":[TD([[makeQuery(id+"F17.imprint","IMPRINT",EDGE,{"derivedFrom":sQuery(id+"F17.wireOp",EDGE,"E35.0")}),-1.0]])]});
            var Q2;
            Q2=makeQuery(id+"F17.imprint","IMPRINT",FACE,{"disambiguationData":[TD([[makeQuery(id+"F17.imprint","IMPRINT",EDGE,{"derivedFrom":sQuery(id+"F17.wireOp",EDGE,"E38.3.0")}),-1.0]])]});
            var Q3;
            Q3=makeQuery(id+"F17.imprint","IMPRINT",FACE,{"disambiguationData":[TD([[makeQuery(id+"F17.imprint","IMPRINT",EDGE,{"derivedFrom":sQuery(id+"F17.wireOp",EDGE,"E38.2.0")}),-1.0]])]});
            var Q4;
            Q4=makeQuery(id+"F17.imprint","IMPRINT",FACE,{"disambiguationData":[TD([[makeQuery(id+"F17.imprint","IMPRINT",EDGE,{"derivedFrom":sQuery(id+"F17.wireOp",EDGE,"E39")}),1.0]])]});
            extrude(context, id + "F18", {"entities" : qUnion([Q0, Q1, Q2, Q3, Q4]), "operationType" : NewBodyOperationType.REMOVE, "oppositeDirection" : true, "depth" : .2 * mm, "offsetDistance" : 25 * mm});
        }
        {
            var Q0;
            Q0=makeQuery(id+"F18.boolean.opBoolean","COPY",EDGE,{"derivedFrom":makeQuery(id+"F18.opExtrude","CAP_EDGE",EDGE,{"disambiguationData":[OSD([sQuery(id+"F17.wireOp",EDGE,"E39")])],"isStart":false})});
            var Q1;
            Q1=makeQuery(id+"F13.opExtrude","CAP_FACE",FACE,{"disambiguationData":[OSD([sQuery(id+"F12.wireOp",EDGE,"E27.0"),sQuery(id+"F12.wireOp",EDGE,"E27.1"),sQuery(id+"F12.wireOp",EDGE,"E27.2"),sQuery(id+"F12.wireOp",EDGE,"E27.3"),sQuery(id+"F12.wireOp",EDGE,"E27.4"),sQuery(id+"F12.wireOp",EDGE,"E27.5"),sQuery(id+"F12.wireOp",EDGE,"E27.6"),sQuery(id+"F12.wireOp",EDGE,"E27.7"),sQuery(id+"F12.wireOp",EDGE,"E27.8"),sQuery(id+"F12.wireOp",EDGE,"E27.9"),sQuery(id+"F12.wireOp",EDGE,"E27.10"),sQuery(id+"F12.wireOp",EDGE,"E27.11"),sQuery(id+"F12.wireOp",EDGE,"E27.12"),sQuery(id+"F12.wireOp",EDGE,"E27.13"),sQuery(id+"F12.wireOp",EDGE,"E27.14"),sQuery(id+"F12.wireOp",EDGE,"E27.15"),sQuery(id+"F12.wireOp",EDGE,"E27.16"),sQuery(id+"F12.wireOp",EDGE,"E27.17"),sQuery(id+"F12.wireOp",EDGE,"E27.18"),sQuery(id+"F12.wireOp",EDGE,"E27.19"),sQuery(id+"F12.wireOp",EDGE,"E27.20"),sQuery(id+"F12.wireOp",EDGE,"E27.21"),sQuery(id+"F12.wireOp",EDGE,"E27.22"),sQuery(id+"F12.wireOp",EDGE,"E27.23")])],"isStart":false});
            var Q2;
            Q2=makeQuery(id+"F18.boolean.opBoolean","COPY",EDGE,{"derivedFrom":makeQuery(id+"F18.opExtrude","CAP_EDGE",EDGE,{"disambiguationData":[OSD([sQuery(id+"F17.wireOp",EDGE,"E38.1.1")])],"isStart":true})});
            var Q3;
            Q3=makeQuery(id+"F18.boolean.opBoolean","COPY",EDGE,{"derivedFrom":makeQuery(id+"F18.opExtrude","CAP_EDGE",EDGE,{"disambiguationData":[OSD([sQuery(id+"F17.wireOp",EDGE,"E38.1.0")])],"isStart":true})});
            var Q4;
            Q4=makeQuery(id+"F18.boolean.opBoolean","COPY",EDGE,{"derivedFrom":makeQuery(id+"F18.opExtrude","CAP_EDGE",EDGE,{"disambiguationData":[OSD([sQuery(id+"F17.wireOp",EDGE,"E38.1.2")])],"isStart":true})});
            var Q5;
            Q5=makeQuery(id+"F18.boolean.opBoolean","COPY",EDGE,{"derivedFrom":makeQuery(id+"F18.opExtrude","SWEPT_EDGE",EDGE,{"disambiguationData":[OSD([sQuery(id+"F17.wireOp",EDGE,"E38.1.0"),sQuery(id+"F17.wireOp",EDGE,"E38.1.1")])]})});
            var Q6;
            Q6=makeQuery(id+"F18.boolean.opBoolean","COPY",EDGE,{"derivedFrom":makeQuery(id+"F18.opExtrude","SWEPT_EDGE",EDGE,{"disambiguationData":[OSD([sQuery(id+"F17.wireOp",EDGE,"E38.1.0"),sQuery(id+"F17.wireOp",EDGE,"E38.1.2")])]})});
            var Q7;
            Q7=makeQuery(id+"F18.boolean.opBoolean","COPY",EDGE,{"derivedFrom":makeQuery(id+"F18.opExtrude","CAP_EDGE",EDGE,{"disambiguationData":[OSD([sQuery(id+"F17.wireOp",EDGE,"E38.1.1")])],"isStart":false})});
            var Q8;
            Q8=makeQuery(id+"F18.boolean.opBoolean","COPY",EDGE,{"derivedFrom":makeQuery(id+"F18.opExtrude","CAP_EDGE",EDGE,{"disambiguationData":[OSD([sQuery(id+"F17.wireOp",EDGE,"E38.1.2")])],"isStart":false})});
            var Q9;
            Q9=makeQuery(id+"F18.boolean.opBoolean","COPY",EDGE,{"derivedFrom":makeQuery(id+"F18.opExtrude","CAP_EDGE",EDGE,{"disambiguationData":[OSD([sQuery(id+"F17.wireOp",EDGE,"E38.1.0")])],"isStart":false})});
            var Q10;
            Q10=makeQuery(id+"F18.boolean.opBoolean","COPY",EDGE,{"derivedFrom":makeQuery(id+"F18.opExtrude","SWEPT_EDGE",EDGE,{"disambiguationData":[OSD([sQuery(id+"F17.wireOp",EDGE,"E38.1.1"),sQuery(id+"F17.wireOp",EDGE,"E38.1.2")])]})});
            var Q11;
            Q11=makeQuery(id+"F18.boolean.opBoolean","COPY",EDGE,{"derivedFrom":makeQuery(id+"F18.opExtrude","CAP_EDGE",EDGE,{"disambiguationData":[OSD([sQuery(id+"F17.wireOp",EDGE,"E35.2")])],"isStart":true})});
            var Q12;
            Q12=makeQuery(id+"F18.boolean.opBoolean","COPY",EDGE,{"derivedFrom":makeQuery(id+"F18.opExtrude","CAP_EDGE",EDGE,{"disambiguationData":[OSD([sQuery(id+"F17.wireOp",EDGE,"E35.0")])],"isStart":true})});
            var Q13;
            Q13=makeQuery(id+"F18.boolean.opBoolean","COPY",EDGE,{"derivedFrom":makeQuery(id+"F18.opExtrude","CAP_EDGE",EDGE,{"disambiguationData":[OSD([sQuery(id+"F17.wireOp",EDGE,"E35.1")])],"isStart":true})});
            var Q14;
            Q14=makeQuery(id+"F18.boolean.opBoolean","COPY",EDGE,{"derivedFrom":makeQuery(id+"F18.opExtrude","CAP_EDGE",EDGE,{"disambiguationData":[OSD([sQuery(id+"F17.wireOp",EDGE,"E35.0")])],"isStart":false})});
            var Q15;
            Q15=makeQuery(id+"F18.boolean.opBoolean","COPY",EDGE,{"derivedFrom":makeQuery(id+"F18.opExtrude","CAP_EDGE",EDGE,{"disambiguationData":[OSD([sQuery(id+"F17.wireOp",EDGE,"E35.2")])],"isStart":false})});
            var Q16;
            Q16=makeQuery(id+"F18.boolean.opBoolean","COPY",EDGE,{"derivedFrom":makeQuery(id+"F18.opExtrude","CAP_EDGE",EDGE,{"disambiguationData":[OSD([sQuery(id+"F17.wireOp",EDGE,"E35.1")])],"isStart":false})});
            var Q17;
            Q17=makeQuery(id+"F18.boolean.opBoolean","COPY",EDGE,{"derivedFrom":makeQuery(id+"F18.opExtrude","SWEPT_EDGE",EDGE,{"disambiguationData":[OSD([sQuery(id+"F17.wireOp",EDGE,"E35.0"),sQuery(id+"F17.wireOp",EDGE,"E35.2")])]})});
            var Q18;
            Q18=makeQuery(id+"F18.boolean.opBoolean","COPY",EDGE,{"derivedFrom":makeQuery(id+"F18.opExtrude","SWEPT_EDGE",EDGE,{"disambiguationData":[OSD([sQuery(id+"F17.wireOp",EDGE,"E35.1"),sQuery(id+"F17.wireOp",EDGE,"E35.2")])]})});
            var Q19;
            Q19=makeQuery(id+"F18.boolean.opBoolean","COPY",EDGE,{"derivedFrom":makeQuery(id+"F18.opExtrude","SWEPT_EDGE",EDGE,{"disambiguationData":[OSD([sQuery(id+"F17.wireOp",EDGE,"E35.0"),sQuery(id+"F17.wireOp",EDGE,"E35.1")])]})});
            var Q20;
            Q20=makeQuery(id+"F18.boolean.opBoolean","COPY",EDGE,{"derivedFrom":makeQuery(id+"F18.opExtrude","CAP_EDGE",EDGE,{"disambiguationData":[OSD([sQuery(id+"F17.wireOp",EDGE,"E38.3.0")])],"isStart":true})});
            var Q21;
            Q21=makeQuery(id+"F18.boolean.opBoolean","COPY",EDGE,{"derivedFrom":makeQuery(id+"F18.opExtrude","CAP_EDGE",EDGE,{"disambiguationData":[OSD([sQuery(id+"F17.wireOp",EDGE,"E38.3.1")])],"isStart":true})});
            var Q22;
            Q22=makeQuery(id+"F18.boolean.opBoolean","COPY",EDGE,{"derivedFrom":makeQuery(id+"F18.opExtrude","CAP_EDGE",EDGE,{"disambiguationData":[OSD([sQuery(id+"F17.wireOp",EDGE,"E38.3.2")])],"isStart":true})});
            var Q23;
            Q23=makeQuery(id+"F18.boolean.opBoolean","COPY",EDGE,{"derivedFrom":makeQuery(id+"F18.opExtrude","SWEPT_EDGE",EDGE,{"disambiguationData":[OSD([sQuery(id+"F17.wireOp",EDGE,"E38.3.1"),sQuery(id+"F17.wireOp",EDGE,"E38.3.2")])]})});
            var Q24;
            Q24=makeQuery(id+"F18.boolean.opBoolean","COPY",EDGE,{"derivedFrom":makeQuery(id+"F18.opExtrude","SWEPT_EDGE",EDGE,{"disambiguationData":[OSD([sQuery(id+"F17.wireOp",EDGE,"E38.3.0"),sQuery(id+"F17.wireOp",EDGE,"E38.3.1")])]})});
            var Q25;
            Q25=makeQuery(id+"F18.boolean.opBoolean","COPY",EDGE,{"derivedFrom":makeQuery(id+"F18.opExtrude","SWEPT_EDGE",EDGE,{"disambiguationData":[OSD([sQuery(id+"F17.wireOp",EDGE,"E38.3.0"),sQuery(id+"F17.wireOp",EDGE,"E38.3.2")])]})});
            var Q26;
            Q26=makeQuery(id+"F18.boolean.opBoolean","COPY",EDGE,{"derivedFrom":makeQuery(id+"F18.opExtrude","CAP_EDGE",EDGE,{"disambiguationData":[OSD([sQuery(id+"F17.wireOp",EDGE,"E38.3.2")])],"isStart":false})});
            var Q27;
            Q27=makeQuery(id+"F18.boolean.opBoolean","COPY",EDGE,{"derivedFrom":makeQuery(id+"F18.opExtrude","CAP_EDGE",EDGE,{"disambiguationData":[OSD([sQuery(id+"F17.wireOp",EDGE,"E38.3.0")])],"isStart":false})});
            var Q28;
            Q28=makeQuery(id+"F18.boolean.opBoolean","COPY",EDGE,{"derivedFrom":makeQuery(id+"F18.opExtrude","CAP_EDGE",EDGE,{"disambiguationData":[OSD([sQuery(id+"F17.wireOp",EDGE,"E38.3.1")])],"isStart":false})});
            var Q29;
            Q29=makeQuery(id+"F18.boolean.opBoolean","COPY",EDGE,{"derivedFrom":makeQuery(id+"F18.opExtrude","CAP_EDGE",EDGE,{"disambiguationData":[OSD([sQuery(id+"F17.wireOp",EDGE,"E38.2.2")])],"isStart":true})});
            var Q30;
            Q30=makeQuery(id+"F18.boolean.opBoolean","COPY",EDGE,{"derivedFrom":makeQuery(id+"F18.opExtrude","CAP_EDGE",EDGE,{"disambiguationData":[OSD([sQuery(id+"F17.wireOp",EDGE,"E38.2.0")])],"isStart":true})});
            var Q31;
            Q31=makeQuery(id+"F18.boolean.opBoolean","COPY",EDGE,{"derivedFrom":makeQuery(id+"F18.opExtrude","CAP_EDGE",EDGE,{"disambiguationData":[OSD([sQuery(id+"F17.wireOp",EDGE,"E38.2.1")])],"isStart":true})});
            var Q32;
            Q32=makeQuery(id+"F18.boolean.opBoolean","COPY",EDGE,{"derivedFrom":makeQuery(id+"F18.opExtrude","CAP_EDGE",EDGE,{"disambiguationData":[OSD([sQuery(id+"F17.wireOp",EDGE,"E38.2.0")])],"isStart":false})});
            var Q33;
            Q33=makeQuery(id+"F18.boolean.opBoolean","COPY",EDGE,{"derivedFrom":makeQuery(id+"F18.opExtrude","CAP_EDGE",EDGE,{"disambiguationData":[OSD([sQuery(id+"F17.wireOp",EDGE,"E38.2.2")])],"isStart":false})});
            var Q34;
            Q34=makeQuery(id+"F18.boolean.opBoolean","COPY",EDGE,{"derivedFrom":makeQuery(id+"F18.opExtrude","SWEPT_EDGE",EDGE,{"disambiguationData":[OSD([sQuery(id+"F17.wireOp",EDGE,"E38.2.1"),sQuery(id+"F17.wireOp",EDGE,"E38.2.2")])]})});
            var Q35;
            Q35=makeQuery(id+"F18.boolean.opBoolean","COPY",EDGE,{"derivedFrom":makeQuery(id+"F18.opExtrude","SWEPT_EDGE",EDGE,{"disambiguationData":[OSD([sQuery(id+"F17.wireOp",EDGE,"E38.2.0"),sQuery(id+"F17.wireOp",EDGE,"E38.2.2")])]})});
            var Q36;
            Q36=makeQuery(id+"F18.boolean.opBoolean","COPY",EDGE,{"derivedFrom":makeQuery(id+"F18.opExtrude","SWEPT_EDGE",EDGE,{"disambiguationData":[OSD([sQuery(id+"F17.wireOp",EDGE,"E38.2.0"),sQuery(id+"F17.wireOp",EDGE,"E38.2.1")])]})});
            var Q37;
            Q37=makeQuery(id+"F18.boolean.opBoolean","COPY",EDGE,{"derivedFrom":makeQuery(id+"F18.opExtrude","CAP_EDGE",EDGE,{"disambiguationData":[OSD([sQuery(id+"F17.wireOp",EDGE,"E38.2.1")])],"isStart":false})});
            fillet(context, id + "F19", {"entities" : qUnion([Q0, Q1, Q2, Q3, Q4, Q5, Q6, Q7, Q8, Q9, Q10, Q11, Q12, Q13, Q14, Q15, Q16, Q17, Q18, Q19, Q20, Q21, Q22, Q23, Q24, Q25, Q26, Q27, Q28, Q29, Q30, Q31, Q32, Q33, Q34, Q35, Q36, Q37]), "radius" : .1 * mm, "tangentPropagation" : true, "allowEdgeOverflow" : false});
        }
    });
